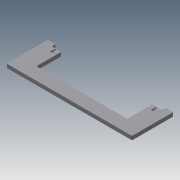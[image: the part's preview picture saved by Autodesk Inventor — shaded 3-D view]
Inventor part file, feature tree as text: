
AUTODESK INVENTOR PART (.ipt)
format: ipt  version: 2014 (Build 180170000, 170)  size: 157,696 bytes
history: native  units: mm
features: extrude x4, sketch x4, mirror x1, fillet x1
ambient origin geometry x8: Origin, YZ Plane, XZ Plane, XY Plane, X Axis, Y Axis, Z Axis, Center Point
bodies: Solid1 (feature_tree)
feature tree (10):
  extrude  "Extrusion1"  Depth=60.0mm
  extrude  "Extrusion2"  Depth=145.0mm
  extrude  "Extrusion3"  Depth=3.0mm TaperAngle=0.0deg
  extrude  "Extrusion4"  Depth=10.0mm TaperAngle=0.0deg
  mirror  "Mirror1"
  fillet  "Fillet1"  Radius=2.1mm
  sketch  "Sketch1"  dims[d0=200.0mm d1=60.0mm]
  sketch  "Sketch2"  dims[d2=6.0mm d3=0.0mm d4=145.0mm]
  sketch  "Sketch3"  dims[d5=20.0mm d6=3.0mm d7=0.0mm]
  sketch  "Sketch4"  dims[d9=6.0mm d10=10.0mm d11=0.0mm d12=2.1mm d13=4.1mm d15=6.0mm d16=1.8mm d17=10.0mm d18=0.0mm d19=1.0mm d20=12.25mm d21=8.0mm d22=9.0mm]
